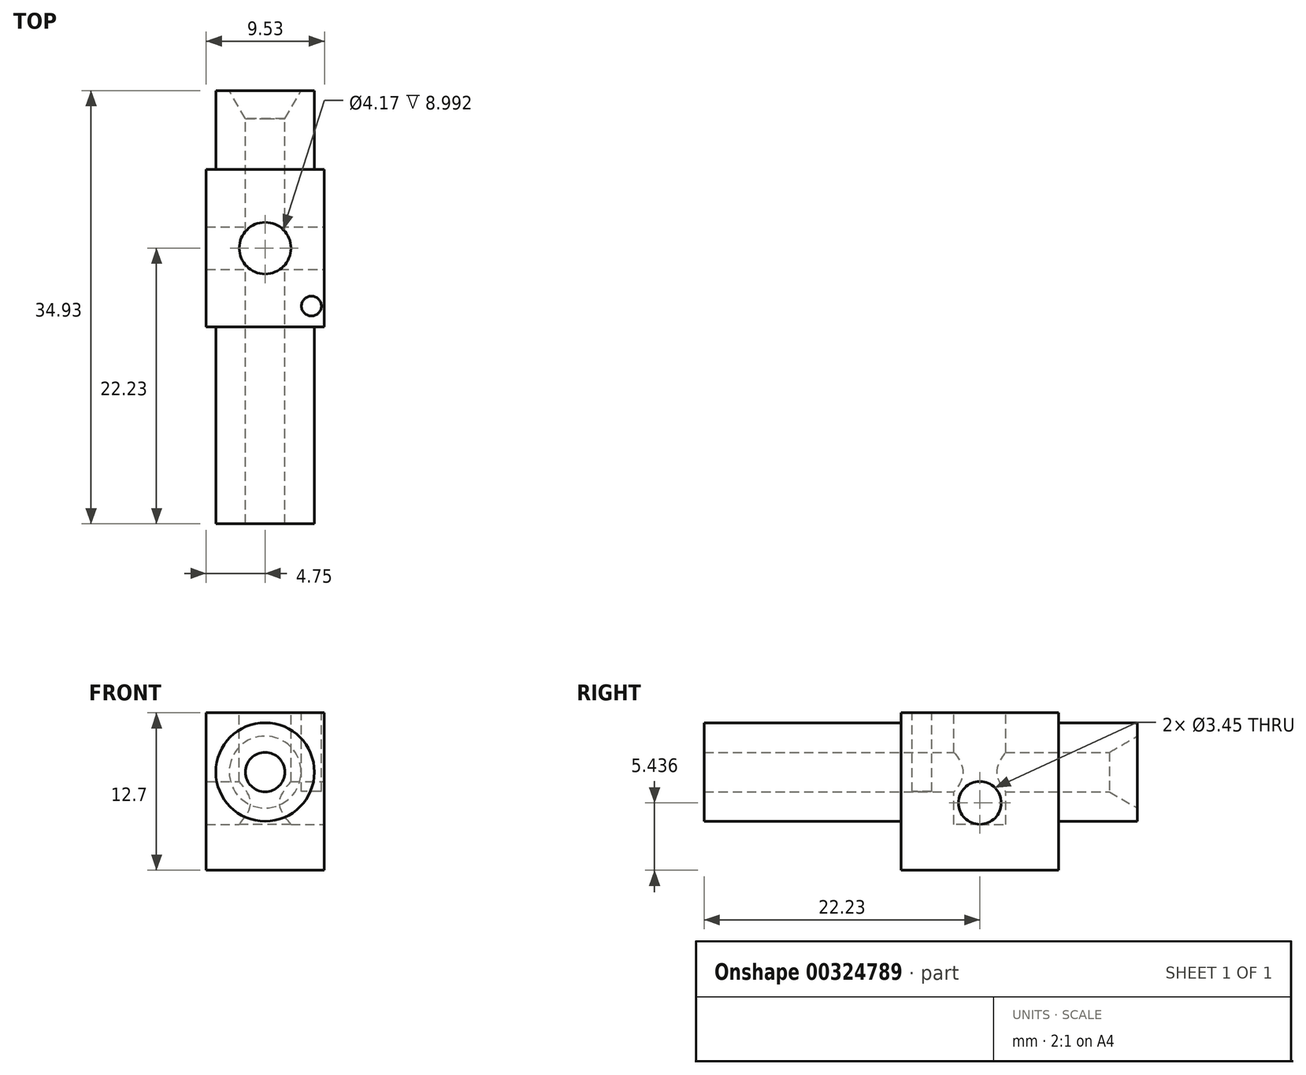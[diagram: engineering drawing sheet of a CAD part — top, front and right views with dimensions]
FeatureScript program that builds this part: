
annotation { "Feature Type Name" : "Feature", "Feature Type Description" : "" }
export const myFeature = defineFeature(function(context is Context, id is Id, definition is map)
    precondition{}
    {
        {
            var Q0;
            Q0=qCreatedBy(makeId("Front.planeOp"),FACE);
            var sketch = newSketch(context, id + "F0", { "sketchPlane" : qUnion([Q0])});
            skLineSegment(sketch, "E0.bottom", {"start": v(-4.75, 0) * mm, "end": v(4.78, 0) * mm});
            skLineSegment(sketch, "E0.top", {"start": v(-4.75, 12.7) * mm, "end": v(4.78, 12.7) * mm});
            skLineSegment(sketch, "E0.left", {"start": v(-4.75, 0) * mm, "end": v(-4.75, 12.7) * mm});
            skLineSegment(sketch, "E0.right", {"start": v(4.78, 0) * mm, "end": v(4.78, 12.7) * mm});
            skSolve(sketch);
        }
        {
            var Q0;
            Q0=makeQuery(id+"F0.imprint","IMPRINT",FACE,{"disambiguationData":[TD([[makeQuery(id+"F0.imprint","IMPRINT",EDGE,{"derivedFrom":sQuery(id+"F0.wireOp",EDGE,"E0.bottom")}),1.0]])]});
            extrude(context, id + "F1", {"entities" : qUnion([Q0]), "depth" : 12.7 * mm, "offsetDistance" : 25.4 * mm});
        }
        {
            var Q0;
            Q0=makeQuery(id+"F1.opExtrude","CAP_FACE",FACE,{"disambiguationData":[OSD([sQuery(id+"F0.wireOp",EDGE,"E0.bottom"),sQuery(id+"F0.wireOp",EDGE,"E0.top"),sQuery(id+"F0.wireOp",EDGE,"E0.left"),sQuery(id+"F0.wireOp",EDGE,"E0.right")])],"isStart":false});
            var sketch = newSketch(context, id + "F2", { "sketchPlane" : qUnion([Q0])});
            skCircle(sketch, "E1", {"center": v(0, 7.92) * mm, "radius": 3.98 * mm});
            skSolve(sketch);
        }
        {
            var Q0;
            Q0=makeQuery(id+"F2.imprint","IMPRINT",FACE,{"disambiguationData":[TD([[makeQuery(id+"F2.imprint","IMPRINT",EDGE,{"derivedFrom":sQuery(id+"F2.wireOp",EDGE,"E1")}),1.0]])]});
            extrude(context, id + "F3", {"entities" : qUnion([Q0]), "operationType" : NewBodyOperationType.ADD, "depth" : 15.88 * mm, "offsetDistance" : 25.4 * mm});
        }
        {
            var Q0;
            Q0=makeQuery(id+"F1.opExtrude","CAP_FACE",FACE,{"disambiguationData":[OSD([sQuery(id+"F0.wireOp",EDGE,"E0.bottom"),sQuery(id+"F0.wireOp",EDGE,"E0.top"),sQuery(id+"F0.wireOp",EDGE,"E0.left"),sQuery(id+"F0.wireOp",EDGE,"E0.right")])],"isStart":true});
            var sketch = newSketch(context, id + "F4", { "sketchPlane" : qUnion([Q0])});
            skCircle(sketch, "E2", {"center": v(0, 7.92) * mm, "radius": 3.98 * mm});
            skSolve(sketch);
        }
        {
            var Q0;
            Q0=makeQuery(id+"F4.imprint","IMPRINT",FACE,{"disambiguationData":[TD([[makeQuery(id+"F4.imprint","IMPRINT",EDGE,{"derivedFrom":sQuery(id+"F4.wireOp",EDGE,"E2")}),1.0]])]});
            extrude(context, id + "F5", {"entities" : qUnion([Q0]), "operationType" : NewBodyOperationType.ADD, "depth" : 6.35 * mm, "offsetDistance" : 25.4 * mm});
        }
        {
            var Q0;
            Q0=makeQuery(id+"F5.opExtrude","CAP_FACE",FACE,{"disambiguationData":[OSD([sQuery(id+"F4.wireOp",EDGE,"E2")])],"isStart":false});
            var sketch = newSketch(context, id + "F6", { "sketchPlane" : qUnion([Q0])});
            skCircle(sketch, "E3", {"center": v(0, 7.92) * mm, "radius": 1.59 * mm});
            skSolve(sketch);
        }
        {
            var Q0;
            Q0=makeQuery(id+"F6.imprint","IMPRINT",FACE,{"disambiguationData":[TD([[makeQuery(id+"F6.imprint","IMPRINT",EDGE,{"derivedFrom":sQuery(id+"F6.wireOp",EDGE,"E3")}),1.0]])]});
            extrude(context, id + "F7", {"entities" : qUnion([Q0]), "operationType" : NewBodyOperationType.REMOVE, "endBound" : BoundingType.THROUGH_ALL, "oppositeDirection" : true, "depth" : 25.4 * mm, "offsetDistance" : 25.4 * mm});
        }
        {
            var Q0;
            Q0=makeQuery(id+"F1.opExtrude","SWEPT_FACE",FACE,{"disambiguationData":[OSD([sQuery(id+"F0.wireOp",EDGE,"E0.right")])]});
            var sketch = newSketch(context, id + "F8", { "sketchPlane" : qUnion([Q0])});
            skCircle(sketch, "E4", {"center": v(-6.35, 5.44) * mm, "radius": 1.73 * mm});
            skSolve(sketch);
        }
        {
            var Q0;
            Q0=makeQuery(id+"F8.imprint","IMPRINT",FACE,{"disambiguationData":[TD([[makeQuery(id+"F8.imprint","IMPRINT",EDGE,{"derivedFrom":sQuery(id+"F8.wireOp",EDGE,"E4")}),1.0]])]});
            extrude(context, id + "F9", {"entities" : qUnion([Q0]), "operationType" : NewBodyOperationType.REMOVE, "endBound" : BoundingType.THROUGH_ALL, "oppositeDirection" : true, "depth" : 25.4 * mm, "offsetDistance" : 25.4 * mm});
        }
        {
            var Q0;
            Q0=makeQuery(id+"F1.opExtrude","SWEPT_FACE",FACE,{"disambiguationData":[OSD([sQuery(id+"F0.wireOp",EDGE,"E0.top")])]});
            var sketch = newSketch(context, id + "F10", { "sketchPlane" : qUnion([Q0])});
            skCircle(sketch, "E5", {"center": v(0, -6.35) * mm, "radius": 2.08 * mm});
            skSolve(sketch);
        }
        {
            var Q0;
            Q0=makeQuery(id+"F10.imprint","IMPRINT",FACE,{"disambiguationData":[TD([[makeQuery(id+"F10.imprint","IMPRINT",EDGE,{"derivedFrom":sQuery(id+"F10.wireOp",EDGE,"E5")}),1.0]])]});
            extrude(context, id + "F11", {"entities" : qUnion([Q0]), "operationType" : NewBodyOperationType.REMOVE, "oppositeDirection" : true, "depth" : 9 * mm, "offsetDistance" : 25.4 * mm});
        }
        {
            var Q0;
            Q0=makeQuery(id+"F1.opExtrude","SWEPT_FACE",FACE,{"disambiguationData":[OSD([sQuery(id+"F0.wireOp",EDGE,"E0.top")])]});
            var sketch = newSketch(context, id + "F12", { "sketchPlane" : qUnion([Q0])});
            skCircle(sketch, "E6", {"center": v(3.73, -11.02) * mm, "radius": 0.8 * mm});
            skSolve(sketch);
        }
        {
            var Q0;
            Q0=makeQuery(id+"F12.imprint","IMPRINT",FACE,{"disambiguationData":[TD([[makeQuery(id+"F12.imprint","IMPRINT",EDGE,{"derivedFrom":sQuery(id+"F12.wireOp",EDGE,"E6")}),1.0]])]});
            extrude(context, id + "F13", {"entities" : qUnion([Q0]), "operationType" : NewBodyOperationType.REMOVE, "oppositeDirection" : true, "depth" : 6.35 * mm, "offsetDistance" : 25.4 * mm});
        }
        {
            var Q0;
            Q0=qCreatedBy(makeId("Right.planeOp"),FACE);
            var sketch = newSketch(context, id + "F14", { "sketchPlane" : qUnion([Q0])});
            skLineSegment(sketch, "E7", {"start": v(-32.3, 7.92) * mm, "end": v(15.54, 7.92) * mm, "construction": true});
            skLineSegment(sketch, "E8", {"start": v(6.39, 10.85) * mm, "end": v(3.84, 9.37) * mm});
            skLineSegment(sketch, "E9", {"start": v(3.84, 9.37) * mm, "end": v(3.84, 7.92) * mm});
            skLineSegment(sketch, "E10", {"start": v(3.84, 7.92) * mm, "end": v(6.39, 7.92) * mm});
            skLineSegment(sketch, "E11", {"start": v(6.39, 7.92) * mm, "end": v(6.39, 10.85) * mm});
            skSolve(sketch);
        }
        {
            var Q0;
            Q0=makeQuery(id+"F14.imprint","IMPRINT",FACE,{"disambiguationData":[TD([[makeQuery(id+"F14.imprint","IMPRINT",EDGE,{"derivedFrom":sQuery(id+"F14.wireOp",EDGE,"E8")}),1.0]])]});
            var Q1;
            Q1=makeQuery(id+"F5.opExtrude","CAP_EDGE",EDGE,{"disambiguationData":[OSD([sQuery(id+"F4.wireOp",EDGE,"E2")])],"isStart":false});
            sweep(context, id + "F15", {"operationType" : NewBodyOperationType.REMOVE, "profiles" : qUnion([Q0]), "path" : qUnion([Q1])});
        }
    });
